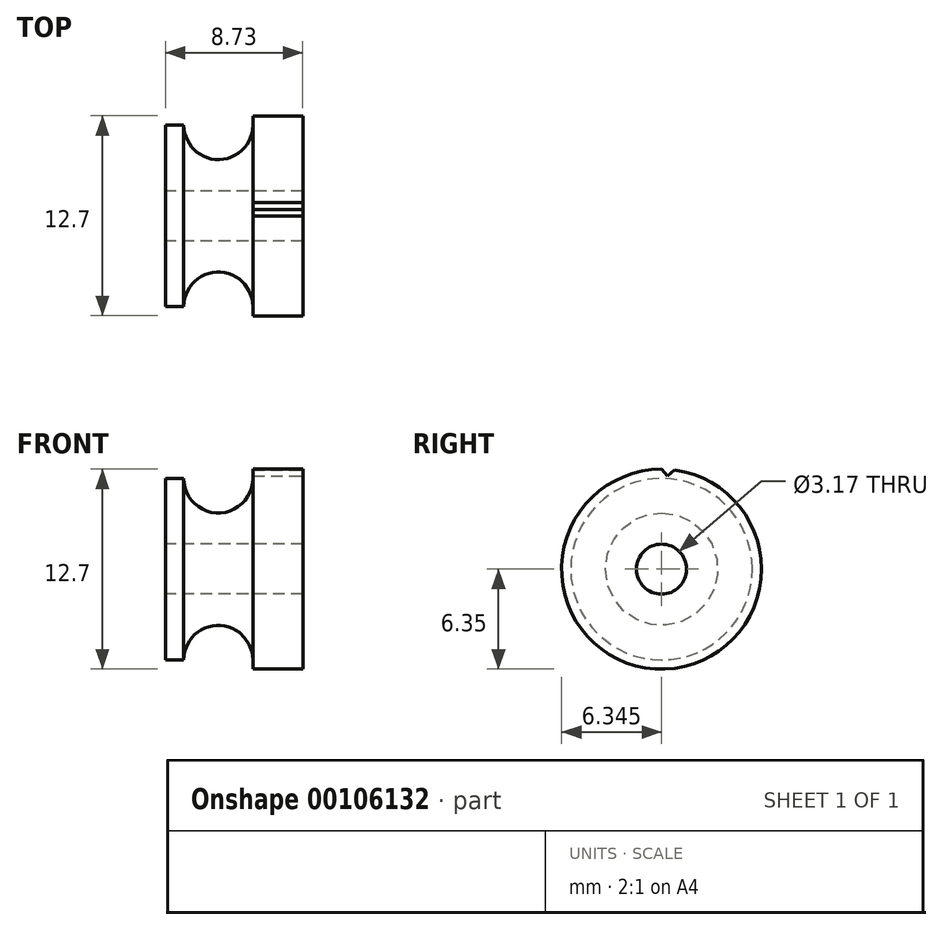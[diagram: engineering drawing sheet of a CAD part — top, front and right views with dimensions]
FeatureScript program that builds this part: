
annotation { "Feature Type Name" : "Feature", "Feature Type Description" : "" }
export const myFeature = defineFeature(function(context is Context, id is Id, definition is map)
    precondition{}
    {
        {
            var Q0;
            Q0=qCreatedBy(makeId("Front.planeOp"),FACE);
            cPlane(context, id + "F0", {"entities" : qUnion([Q0]), "cplaneType" : CPlaneType.OFFSET, "offset" : 60.32 * mm, "width" : 152.4 * mm, "height" : 152.4 * mm});
        }
        {
            var Q0;
            Q0=qCreatedBy(id+"F0.planeOp",FACE);
            var sketch = newSketch(context, id + "F1", { "sketchPlane" : qUnion([Q0])});
            skLineSegment(sketch, "E0", {"start": v(-19.05, 0) * mm, "end": v(19.05, 0) * mm, "construction": true});
            skLineSegment(sketch, "E1", {"start": v(19.05, 1.59) * mm, "end": v(27.78, 1.59) * mm});
            skLineSegment(sketch, "E2", {"start": v(27.78, 1.59) * mm, "end": v(27.78, 6.35) * mm});
            skLineSegment(sketch, "E3", {"start": v(27.78, 6.35) * mm, "end": v(24.6, 6.35) * mm});
            skLineSegment(sketch, "E4", {"start": v(24.6, 6.35) * mm, "end": v(24.6, 5.76) * mm});
            skLineSegment(sketch, "E5", {"start": v(24.6, 5.76) * mm, "end": v(20.22, 5.76) * mm, "construction": true});
            skLineSegment(sketch, "E6", {"start": v(20.22, 5.76) * mm, "end": v(19.05, 5.76) * mm});
            skLineSegment(sketch, "E7", {"start": v(19.05, 5.76) * mm, "end": v(19.05, 1.59) * mm});
            skArc(sketch, "E8", {"start": v(20.22, 5.76) * mm, "mid": v(22.42, 3.57) * mm, "end": v(24.6, 5.76) * mm});
            skSolve(sketch);
        }
        {
            var Q0;
            Q0 = qSketchRegion(id + "F1", true);
            var Q1;
            Q1=sQuery(id+"F1.wireOp",EDGE,"E0");
            revolve(context, id + "F2", {"entities" : qUnion([Q0]), "axis" : qUnion([Q1]), "revolveType" : RevolveType.FULL});
        }
        {
            var Q0;
            Q0=makeQuery(id+"F2.opRevolve","SWEPT_FACE",FACE,{"disambiguationData":[OSD([sQuery(id+"F1.wireOp",EDGE,"E2")])]});
            var sketch = newSketch(context, id + "F3", { "sketchPlane" : qUnion([Q0])});
            skLineSegment(sketch, "E9", {"start": v(-60.33, 0) * mm, "end": v(-60.33, 6.35) * mm, "construction": true});
            skLineSegment(sketch, "E10", {"start": v(-60.33, 0) * mm, "end": v(-59.9, 6.34) * mm, "construction": true});
            skLineSegment(sketch, "E11", {"start": v(-60.33, 6.35) * mm, "end": v(-59.94, 5.92) * mm});
            skLineSegment(sketch, "E12.MirrorCS", {"start": v(-59.5, 6.3) * mm, "end": v(-59.94, 5.92) * mm});
            skArc(sketch, "E13", {"start": v(-59.5, 6.3) * mm, "mid": v(-59.9, 6.34) * mm, "end": v(-60.33, 6.35) * mm});
            skSolve(sketch);
        }
        {
            var Q0;
            Q0 = qSketchRegion(id + "F3", true);
            var Q1;
            Q1=makeQuery(id+"F2.opRevolve","SWEPT_FACE",FACE,{"disambiguationData":[OSD([sQuery(id+"F1.wireOp",EDGE,"E4")])]});
            extrude(context, id + "F4", {"entities" : qUnion([Q0]), "operationType" : NewBodyOperationType.REMOVE, "endBound" : BoundingType.UP_TO_SURFACE, "oppositeDirection" : true, "endBoundEntityFace" : qUnion([Q1]), "depth" : 25.4 * mm});
        }
    });
